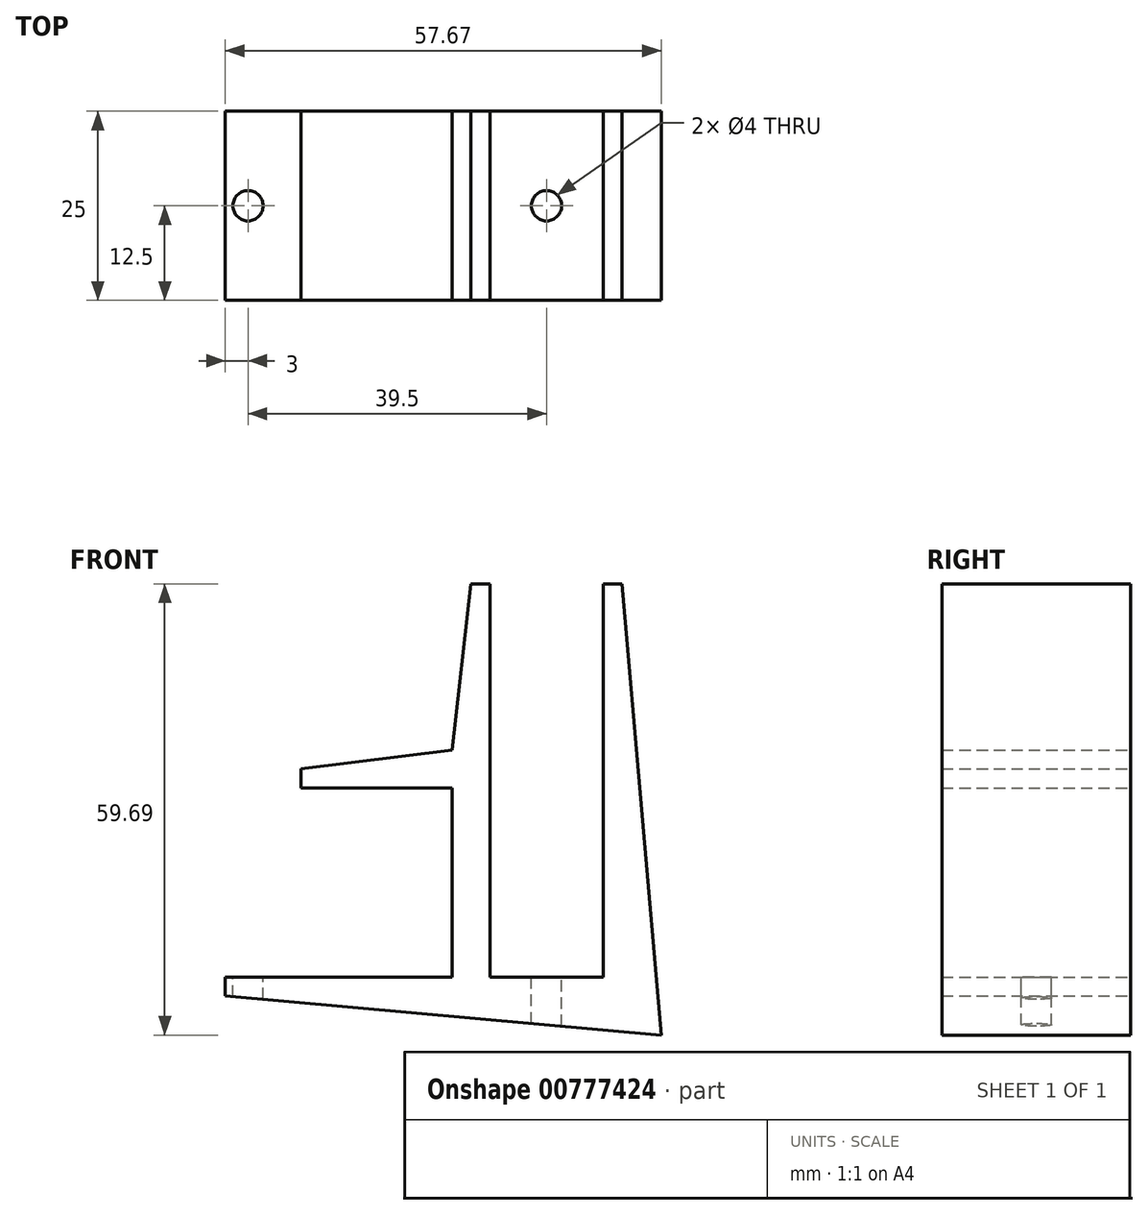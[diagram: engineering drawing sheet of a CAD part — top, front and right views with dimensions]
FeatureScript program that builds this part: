
annotation { "Feature Type Name" : "Feature", "Feature Type Description" : "" }
export const myFeature = defineFeature(function(context is Context, id is Id, definition is map)
    precondition{}
    {
        {
            var Q0;
            Q0=qCreatedBy(makeId("Front.planeOp"),FACE);
            var sketch = newSketch(context, id + "F0", { "sketchPlane" : qUnion([Q0])});
            skLineSegment(sketch, "E0", {"start": v(-30, 0) * mm, "end": v(0, 0) * mm});
            skLineSegment(sketch, "E1", {"start": v(0, 0) * mm, "end": v(0, 25) * mm});
            skLineSegment(sketch, "E2", {"start": v(0, 25) * mm, "end": v(-20, 25) * mm});
            skLineSegment(sketch, "E3", {"start": v(-20, 25) * mm, "end": v(-20, 27.5) * mm});
            skLineSegment(sketch, "E4", {"start": v(-20, 27.5) * mm, "end": v(0, 30) * mm});
            skLineSegment(sketch, "E5", {"start": v(0, 30) * mm, "end": v(2.5, 52) * mm});
            skLineSegment(sketch, "E6", {"start": v(2.5, 52) * mm, "end": v(5, 52) * mm});
            skLineSegment(sketch, "E7", {"start": v(5, 52) * mm, "end": v(5, 0) * mm});
            skLineSegment(sketch, "E8", {"start": v(5, 0) * mm, "end": v(20, 0) * mm});
            skLineSegment(sketch, "E9", {"start": v(20, 0) * mm, "end": v(20, 52) * mm});
            skLineSegment(sketch, "E10", {"start": v(20, 52) * mm, "end": v(22.5, 52) * mm});
            skLineSegment(sketch, "E11", {"start": v(22.5, 52) * mm, "end": v(27.67, -7.69) * mm});
            skLineSegment(sketch, "E12", {"start": v(27.67, -7.69) * mm, "end": v(-30, -2.5) * mm});
            skLineSegment(sketch, "E13", {"start": v(-30, -2.5) * mm, "end": v(-30, 0) * mm});
            skLineSegment(sketch, "E14", {"start": v(20, 0) * mm, "end": v(27, 0) * mm, "construction": true});
            skLineSegment(sketch, "E15", {"start": v(20, 0) * mm, "end": v(20, -7) * mm, "construction": true});
            skSolve(sketch);
        }
        {
            var Q0;
            Q0 = qSketchRegion(id + "F0", true);
            extrude(context, id + "F1", {"entities" : qUnion([Q0]), "endBound" : BoundingType.SYMMETRIC, "depth" : 25 * mm, "offsetDistance" : 25 * mm});
        }
        {
            var Q0;
            Q0=qCreatedBy(makeId("Top.planeOp"),FACE);
            var sketch = newSketch(context, id + "F2", { "sketchPlane" : qUnion([Q0])});
            skLineSegment(sketch, "E16", {"start": v(5, 0) * mm, "end": v(20, 0) * mm, "construction": true});
            skCircle(sketch, "E17", {"center": v(-27, 0) * mm, "radius": 2 * mm});
            skCircle(sketch, "E18", {"center": v(12.5, 0) * mm, "radius": 2 * mm});
            skSolve(sketch);
        }
        {
            var Q0;
            Q0 = qSketchRegion(id + "F2", true);
            extrude(context, id + "F3", {"entities" : qUnion([Q0]), "operationType" : NewBodyOperationType.REMOVE, "oppositeDirection" : true, "depth" : 25 * mm, "offsetDistance" : 25 * mm});
        }
    });
